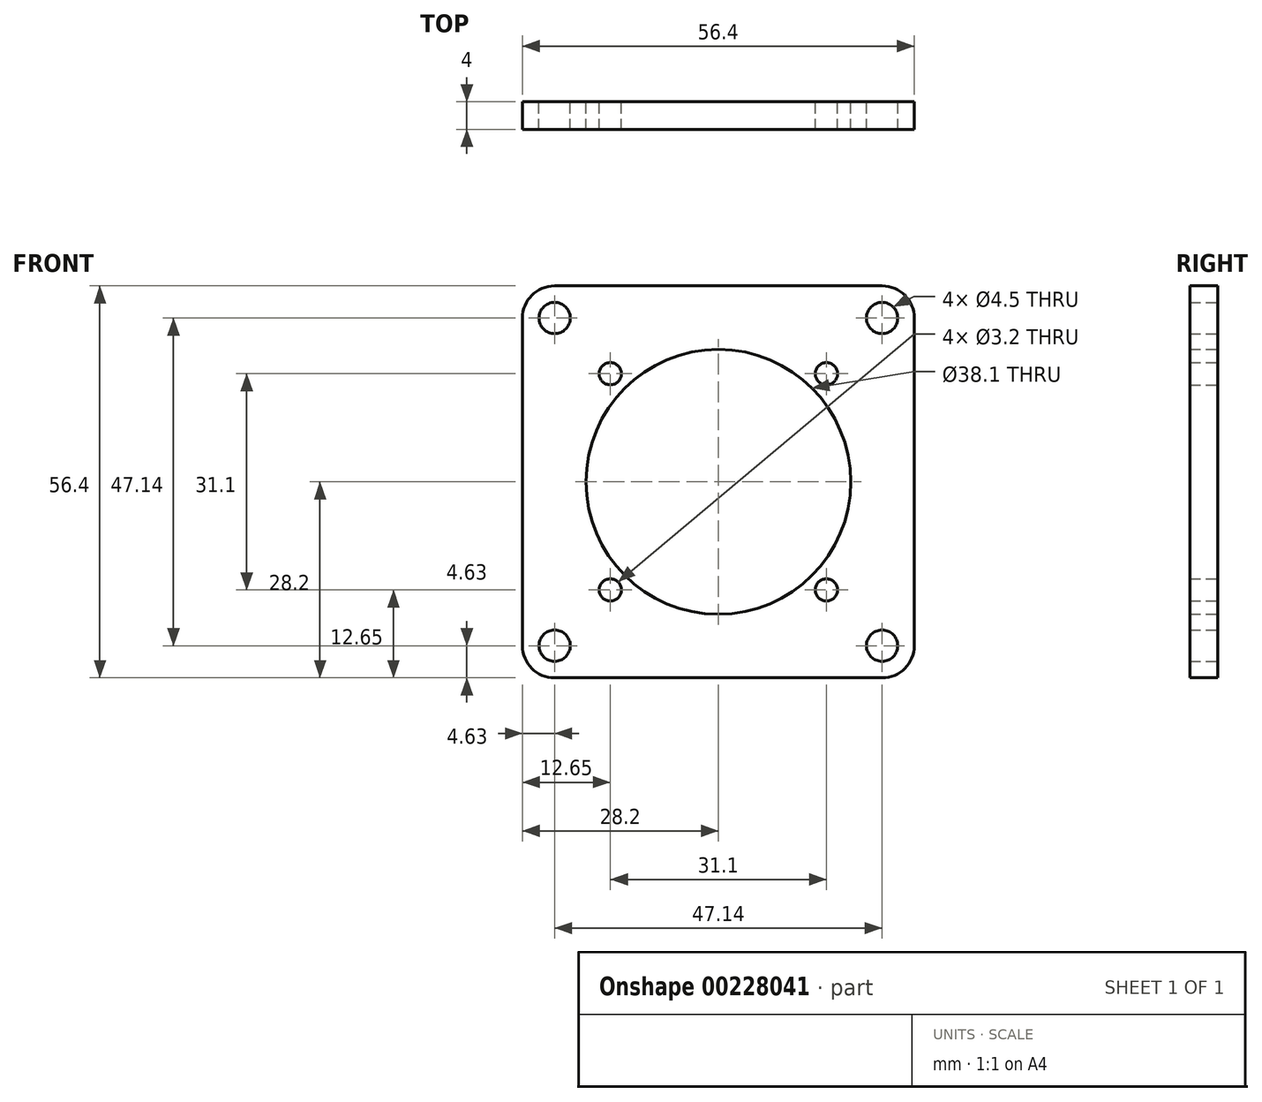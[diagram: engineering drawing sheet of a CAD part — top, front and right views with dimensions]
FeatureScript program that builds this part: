
annotation { "Feature Type Name" : "Feature", "Feature Type Description" : "" }
export const myFeature = defineFeature(function(context is Context, id is Id, definition is map)
    precondition{}
    {
        {
            var Q0;
            Q0=qCreatedBy(makeId("Front.planeOp"),FACE);
            var sketch = newSketch(context, id + "F0", { "sketchPlane" : qUnion([Q0])});
            skLineSegment(sketch, "E0.bottom", {"start": v(23.57, -28.2) * mm, "end": v(-23.57, -28.2) * mm});
            skLineSegment(sketch, "E0.top", {"start": v(23.57, 28.2) * mm, "end": v(-23.57, 28.2) * mm});
            skLineSegment(sketch, "E0.left", {"start": v(28.2, -23.57) * mm, "end": v(28.2, 23.57) * mm});
            skLineSegment(sketch, "E0.right", {"start": v(-28.2, -23.57) * mm, "end": v(-28.2, 23.57) * mm});
            skPoint(sketch, "E0.middle", {"position": v(0, 0) * mm});
            skPoint(sketch, "E1.visualSharp", {"position": v(-28.2, 28.2) * mm});
            skArc(sketch, "E1.filletArc", {"start": v(-23.57, 28.2) * mm, "mid": v(-26.84, 26.84) * mm, "end": v(-28.2, 23.57) * mm});
            skPoint(sketch, "E2.visualSharp", {"position": v(28.2, 28.2) * mm});
            skArc(sketch, "E2.filletArc", {"start": v(28.2, 23.57) * mm, "mid": v(26.84, 26.84) * mm, "end": v(23.57, 28.2) * mm});
            skPoint(sketch, "E3.visualSharp", {"position": v(28.2, -28.2) * mm});
            skArc(sketch, "E3.filletArc", {"start": v(23.57, -28.2) * mm, "mid": v(26.84, -26.84) * mm, "end": v(28.2, -23.57) * mm});
            skPoint(sketch, "E4.visualSharp", {"position": v(-28.2, -28.2) * mm});
            skArc(sketch, "E4.filletArc", {"start": v(-28.2, -23.57) * mm, "mid": v(-26.84, -26.84) * mm, "end": v(-23.57, -28.2) * mm});
            skCircle(sketch, "E5", {"center": v(0, 0) * mm, "radius": 19.05 * mm});
            skLineSegment(sketch, "E6", {"start": v(-28.2, 28.2) * mm, "end": v(28.2, -28.2) * mm, "construction": true});
            skLineSegment(sketch, "E7", {"start": v(-28.2, -28.2) * mm, "end": v(28.2, 28.2) * mm, "construction": true});
            skCircle(sketch, "E8", {"center": v(-23.57, 23.57) * mm, "radius": 2.25 * mm});
            skCircle(sketch, "E9", {"center": v(23.57, 23.57) * mm, "radius": 2.25 * mm});
            skCircle(sketch, "E10", {"center": v(23.57, -23.57) * mm, "radius": 2.25 * mm});
            skCircle(sketch, "E11", {"center": v(-23.57, -23.57) * mm, "radius": 2.25 * mm});
            skCircle(sketch, "E12", {"center": v(-15.55, -15.55) * mm, "radius": 1.6 * mm});
            skCircle(sketch, "E13", {"center": v(-15.55, 15.55) * mm, "radius": 1.6 * mm});
            skCircle(sketch, "E14", {"center": v(15.55, 15.55) * mm, "radius": 1.6 * mm});
            skCircle(sketch, "E15", {"center": v(15.55, -15.55) * mm, "radius": 1.6 * mm});
            skLineSegment(sketch, "E16", {"start": v(-23.57, 23.57) * mm, "end": v(23.57, 23.57) * mm, "construction": true});
            skLineSegment(sketch, "E17", {"start": v(23.57, -23.57) * mm, "end": v(-23.57, -23.57) * mm, "construction": true});
            skLineSegment(sketch, "E18", {"start": v(23.57, -23.57) * mm, "end": v(23.57, 23.57) * mm, "construction": true});
            skLineSegment(sketch, "E19", {"start": v(15.55, 15.55) * mm, "end": v(-15.55, 15.55) * mm, "construction": true});
            skLineSegment(sketch, "E20", {"start": v(-15.55, -15.55) * mm, "end": v(15.55, -15.55) * mm, "construction": true});
            skLineSegment(sketch, "E21", {"start": v(15.55, -15.55) * mm, "end": v(15.55, 15.55) * mm, "construction": true});
            skSolve(sketch);
        }
        {
            var Q0;
            Q0=makeQuery(id+"F0.imprint","IMPRINT",FACE,{"disambiguationData":[TD([[makeQuery(id+"F0.imprint","IMPRINT",EDGE,{"derivedFrom":sQuery(id+"F0.wireOp",EDGE,"E0.bottom")}),-1.0]])]});
            extrude(context, id + "F1", {"entities" : qUnion([Q0]), "depth" : 4 * mm});
        }
    });
